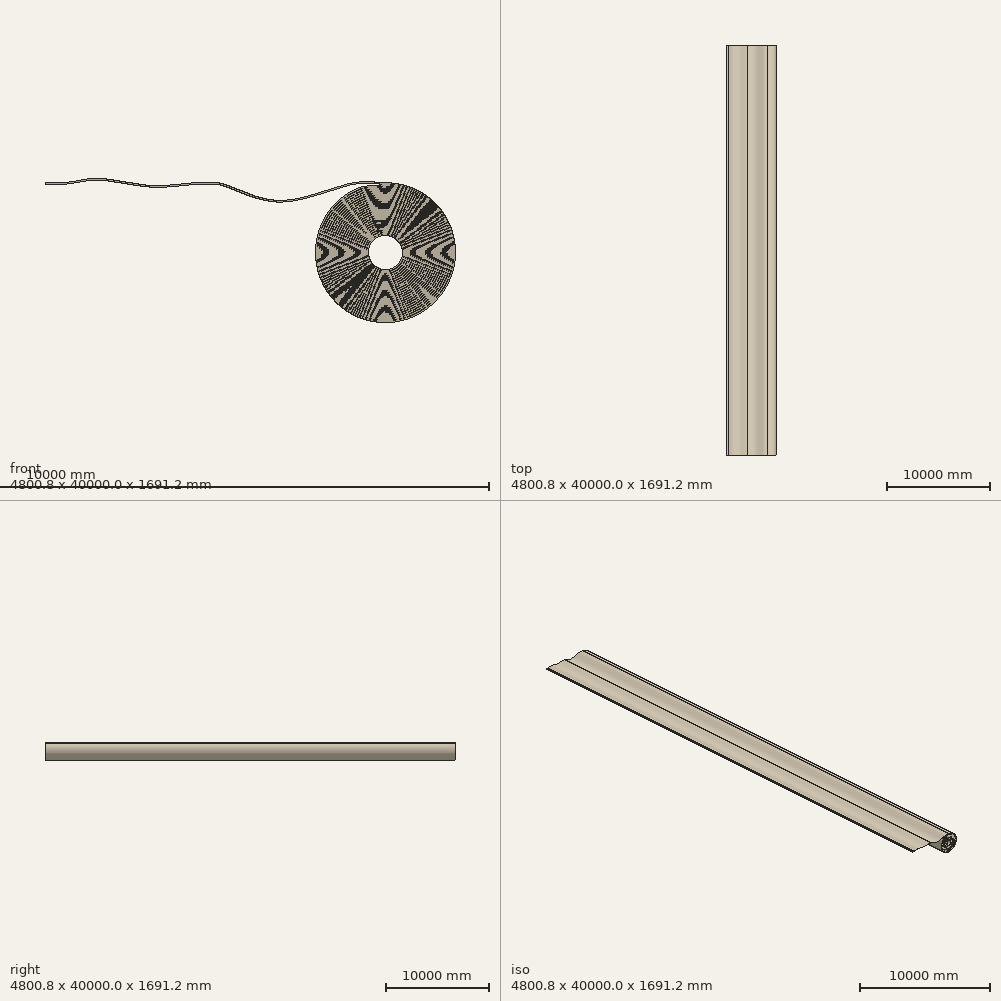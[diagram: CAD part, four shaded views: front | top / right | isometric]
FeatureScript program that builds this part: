
annotation { "Feature Type Name" : "Feature", "Feature Type Description" : "" }
export const myFeature = defineFeature(function(context is Context, id is Id, definition is map)
    precondition{}
    {
        {
            var Q0;
            Q0=qCreatedBy(makeId("Front.planeOp"),FACE);
            var sketch = newSketch(context, id + "F0", { "sketchPlane" : qUnion([Q0])});
            skLineSegment(sketch, "E0", {"start": v(-1454.5, 0) * mm, "end": v(-1283.8, 0) * mm});
            skFitSpline(sketch, "E1", {"points": [v(545.5, 0) * mm, v(1228.86, -205.21) * mm, v(2155.56, 0) * mm, v(2545.5, 0) * mm], "startDerivative": vector(1068.45, 0) * mm, "endDerivative": vector(1156.29, 20.17) * mm});
            skArc(sketch, "E2", {"start": v(2242.52, -51.78) * mm, "mid": v(2661.05, -1588.33) * mm, "end": v(2545.5, 0) * mm});
            skArc(sketch, "E3", {"start": v(2480.79, -605.01) * mm, "mid": v(2539.7, -999.32) * mm, "end": v(2545.3, -600.67) * mm});
            skArc(sketch, "E4", {"start": v(2252.73, -74.65) * mm, "mid": v(2716.15, -1551.15) * mm, "end": v(2422.52, -31.75) * mm});
            skArc(sketch, "E5", {"start": v(2265.35, -96.62) * mm, "mid": v(2704.7, -1528.24) * mm, "end": v(2432.73, -55.63) * mm});
            skArc(sketch, "E6", {"start": v(2296.13, -191.88) * mm, "mid": v(2671.8, -1433.27) * mm, "end": v(2468.1, -152.38) * mm});
            skArc(sketch, "E7", {"start": v(2311.7, -239.45) * mm, "mid": v(2656.21, -1385.53) * mm, "end": v(2483.8, -201.27) * mm});
            skArc(sketch, "E8", {"start": v(2330.08, -285.95) * mm, "mid": v(2638.4, -1338.22) * mm, "end": v(2501.1, -250.35) * mm});
            skArc(sketch, "E9", {"start": v(2270.13, -121.53) * mm, "mid": v(2696.14, -1504.6) * mm, "end": v(2445.35, -79.3) * mm});
            skArc(sketch, "E10", {"start": v(2278.47, -145.1) * mm, "mid": v(2689.56, -1480.46) * mm, "end": v(2450.13, -103.92) * mm});
            skArc(sketch, "E11", {"start": v(2288.1, -168.19) * mm, "mid": v(2680.58, -1456.9) * mm, "end": v(2458.47, -128.18) * mm});
            skArc(sketch, "E12", {"start": v(2303.8, -215.7) * mm, "mid": v(2663.97, -1409.41) * mm, "end": v(2476.13, -176.78) * mm});
            skArc(sketch, "E13", {"start": v(2321.1, -262.62) * mm, "mid": v(2647.56, -1361.83) * mm, "end": v(2491.7, -225.8) * mm});
            skArc(sketch, "E14", {"start": v(2334.03, -311.23) * mm, "mid": v(2632.06, -1314) * mm, "end": v(2510.08, -275.02) * mm});
            skArc(sketch, "E15", {"start": v(2348.93, -332.28) * mm, "mid": v(2622.45, -1290.43) * mm, "end": v(2514.03, -299.92) * mm});
            skArc(sketch, "E16", {"start": v(2357.64, -355.71) * mm, "mid": v(2610.7, -1267.2) * mm, "end": v(2528.93, -324.78) * mm});
            skArc(sketch, "E17", {"start": v(2366.27, -379.18) * mm, "mid": v(2602.03, -1243.35) * mm, "end": v(2537.64, -349.91) * mm});
            skArc(sketch, "E18", {"start": v(2368.44, -405.17) * mm, "mid": v(2596.8, -1218.88) * mm, "end": v(2546.27, -375.24) * mm});
            skArc(sketch, "E19", {"start": v(2375.13, -429.42) * mm, "mid": v(2592.39, -1194.27) * mm, "end": v(2548.44, -400.38) * mm});
            skArc(sketch, "E20", {"start": v(2380.2, -454.4) * mm, "mid": v(2586.6, -1169.89) * mm, "end": v(2555.13, -425.88) * mm});
            skArc(sketch, "E21", {"start": v(2394.28, -475.61) * mm, "mid": v(2576.79, -1146.1) * mm, "end": v(2560.2, -451.42) * mm});
            skArc(sketch, "E22", {"start": v(2398.74, -500.84) * mm, "mid": v(2577.57, -1120.7) * mm, "end": v(2554.28, -475.98) * mm});
            skArc(sketch, "E23", {"start": v(2403.66, -525.97) * mm, "mid": v(2572.98, -1096.11) * mm, "end": v(2558.74, -501.53) * mm});
            skArc(sketch, "E24", {"start": v(2417.42, -547.23) * mm, "mid": v(2563.37, -1072.26) * mm, "end": v(2563.66, -527.32) * mm});
            skArc(sketch, "E25", {"start": v(2431.23, -568.54) * mm, "mid": v(2559.32, -1047.58) * mm, "end": v(2557.42, -551.72) * mm});
            skArc(sketch, "E26", {"start": v(2445.3, -589.85) * mm, "mid": v(2555.12, -1022.91) * mm, "end": v(2551.23, -576.16) * mm});
            skFitSpline(sketch, "E27", {"points": [v(2242.52, -51.78) * mm, v(2422.52, -31.75) * mm], "startDerivative": vector(183.93, 61.4) * mm, "endDerivative": vector(153.02, 25.9) * mm});
            skFitSpline(sketch, "E28", {"points": [v(2252.73, -74.65) * mm, v(2432.73, -55.63) * mm], "startDerivative": vector(180.32, 59.73) * mm, "endDerivative": vector(156.49, 25.3) * mm});
            skFitSpline(sketch, "E29", {"points": [v(2265.35, -96.62) * mm, v(2445.35, -79.3) * mm], "startDerivative": vector(157.48, 51.92) * mm, "endDerivative": vector(138.8, 26.35) * mm});
            skFitSpline(sketch, "E30", {"points": [v(2270.13, -121.53) * mm, v(2450.13, -103.92) * mm], "startDerivative": vector(147.61, 49.78) * mm, "endDerivative": vector(149.7, 21.86) * mm});
            skFitSpline(sketch, "E31", {"points": [v(2278.47, -145.1) * mm, v(2458.47, -128.18) * mm], "startDerivative": vector(145.35, 49.03) * mm, "endDerivative": vector(142.65, 19.55) * mm});
            skFitSpline(sketch, "E32", {"points": [v(2288.1, -168.19) * mm, v(2468.1, -152.38) * mm], "startDerivative": vector(136.5, 46) * mm, "endDerivative": vector(134.79, 16.86) * mm});
            skFitSpline(sketch, "E33", {"points": [v(2296.13, -191.88) * mm, v(2476.13, -176.78) * mm], "startDerivative": vector(141.39, 47.43) * mm, "endDerivative": vector(141.01, 16.75) * mm});
            skFitSpline(sketch, "E34", {"points": [v(2303.8, -215.7) * mm, v(2483.8, -201.27) * mm], "startDerivative": vector(129, 43.84) * mm, "endDerivative": vector(124.28, 13.17) * mm});
            skFitSpline(sketch, "E35", {"points": [v(2311.7, -239.45) * mm, v(2491.7, -225.8) * mm], "startDerivative": vector(119.14, 40.9) * mm, "endDerivative": vector(114.47, 10.73) * mm});
            skFitSpline(sketch, "E36", {"points": [v(2321.1, -262.62) * mm, v(2501.1, -250.35) * mm], "startDerivative": vector(112.96, 38.72) * mm, "endDerivative": vector(112.88, 9.06) * mm});
            skFitSpline(sketch, "E37", {"points": [v(2330.08, -285.95) * mm, v(2510.08, -275.02) * mm], "startDerivative": vector(97.73, 33.85) * mm, "endDerivative": vector(114.93, 7.76) * mm});
            skFitSpline(sketch, "E38", {"points": [v(2334.03, -311.23) * mm, v(2514.03, -299.92) * mm], "startDerivative": vector(96.73, 34.47) * mm, "endDerivative": vector(104.3, 6.2) * mm});
            skFitSpline(sketch, "E39", {"points": [v(2348.93, -332.28) * mm, v(2528.93, -324.78) * mm], "startDerivative": vector(104.34, 35.26) * mm, "endDerivative": vector(98.4, 2.85) * mm});
            skFitSpline(sketch, "E40", {"points": [v(2357.64, -355.71) * mm, v(2537.64, -349.91) * mm], "startDerivative": vector(81.1, 28.03) * mm, "endDerivative": vector(89.55, 0.7) * mm});
            skFitSpline(sketch, "E41", {"points": [v(2366.27, -379.18) * mm, v(2546.27, -375.24) * mm], "startDerivative": vector(85.71, 29.35) * mm, "endDerivative": vector(93.78, -0.96) * mm});
            skFitSpline(sketch, "E42", {"points": [v(2368.44, -405.17) * mm, v(2548.44, -400.38) * mm], "startDerivative": vector(85.5, 30.71) * mm, "endDerivative": vector(80.17, -1.76) * mm});
            skFitSpline(sketch, "E43", {"points": [v(2375.13, -429.42) * mm, v(2555.13, -425.88) * mm], "startDerivative": vector(81.72, 29.94) * mm, "endDerivative": vector(84.05, -3.33) * mm});
            skFitSpline(sketch, "E44", {"points": [v(2380.2, -454.4) * mm, v(2560.2, -451.42) * mm], "startDerivative": vector(80.36, 30.43) * mm, "endDerivative": vector(77.15, -4.65) * mm});
            skFitSpline(sketch, "E45", {"points": [v(2394.28, -475.61) * mm, v(2554.28, -475.98) * mm], "startDerivative": vector(76.12, 27.62) * mm, "endDerivative": vector(69.22, -3.51) * mm});
            skFitSpline(sketch, "E46", {"points": [v(2398.74, -500.84) * mm, v(2558.74, -501.53) * mm], "startDerivative": vector(68.77, 26.32) * mm, "endDerivative": vector(77.85, -5.07) * mm});
            skFitSpline(sketch, "E47", {"points": [v(2403.66, -525.97) * mm, v(2563.66, -527.32) * mm], "startDerivative": vector(70.8, 28.17) * mm, "endDerivative": vector(68.79, -6.52) * mm});
            skFitSpline(sketch, "E48", {"points": [v(2417.42, -547.23) * mm, v(2557.42, -551.72) * mm], "startDerivative": vector(68.59, 26.01) * mm, "endDerivative": vector(69.01, -5.45) * mm});
            skFitSpline(sketch, "E49", {"points": [v(2431.23, -568.54) * mm, v(2551.23, -576.16) * mm], "startDerivative": vector(61.45, 22.18) * mm, "endDerivative": vector(64.9, -4.09) * mm});
            skFitSpline(sketch, "E50", {"points": [v(2445.3, -589.85) * mm, v(2545.3, -600.67) * mm], "startDerivative": vector(53.88, 18.22) * mm, "endDerivative": vector(56.63, -2.72) * mm});
            skFitSpline(sketch, "E51", {"points": [v(545.5, 0) * mm, v(290.37, 0) * mm, v(-223.77, -32.7) * mm, v(-866.4, 51.44) * mm, v(-1283.8, 0) * mm], "startDerivative": vector(-2021.3, 0) * mm, "endDerivative": vector(-2066.32, 0) * mm});
            skSolve(sketch);
        }
        {
            var Q0;
            Q0=sQuery(id+"F0.wireOp",VERTEX,"E0.start");
            var Q1;
            Q1=qCreatedBy(makeId("Right.planeOp"),FACE);
            cPlane(context, id + "F1", {"entities" : qUnion([Q0, Q1]), "cplaneType" : CPlaneType.PLANE_POINT, "offset" : 25 * mm, "width" : 150 * mm, "height" : 150 * mm});
        }
        {
            var Q0;
            Q0=qCreatedBy(id+"F1.planeOp",FACE);
            var sketch = newSketch(context, id + "F2", { "sketchPlane" : qUnion([Q0])});
            skLineSegment(sketch, "E52.bottom", {"start": v(0, 0) * mm, "end": v(40000, 0) * mm});
            skLineSegment(sketch, "E52.top", {"start": v(0, 20) * mm, "end": v(40000, 20) * mm});
            skLineSegment(sketch, "E52.left", {"start": v(0, 0) * mm, "end": v(0, 20) * mm});
            skLineSegment(sketch, "E52.right", {"start": v(40000, 0) * mm, "end": v(40000, 20) * mm});
            skSolve(sketch);
        }
        {
            var Q0;
            Q0=makeQuery(id+"F2.imprint","IMPRINT",FACE,{"disambiguationData":[TD([[makeQuery(id+"F2.imprint","IMPRINT",EDGE,{"derivedFrom":sQuery(id+"F2.wireOp",EDGE,"E52.bottom")}),1.0]])]});
            var Q1;
            Q1=sQuery(id+"F0.wireOp",EDGE,"E0");
            var Q2;
            Q2=sQuery(id+"F0.wireOp",EDGE,"E1");
            var Q3;
            Q3=sQuery(id+"F0.wireOp",EDGE,"E2");
            var Q4;
            Q4=sQuery(id+"F0.wireOp",EDGE,"E27");
            var Q5;
            Q5=sQuery(id+"F0.wireOp",EDGE,"E4");
            var Q6;
            Q6=sQuery(id+"F0.wireOp",EDGE,"E28");
            var Q7;
            Q7=sQuery(id+"F0.wireOp",EDGE,"E5");
            var Q8;
            Q8=sQuery(id+"F0.wireOp",EDGE,"E29");
            var Q9;
            Q9=sQuery(id+"F0.wireOp",EDGE,"E9");
            var Q10;
            Q10=sQuery(id+"F0.wireOp",EDGE,"E30");
            var Q11;
            Q11=sQuery(id+"F0.wireOp",EDGE,"E10");
            var Q12;
            Q12=sQuery(id+"F0.wireOp",EDGE,"E31");
            var Q13;
            Q13=sQuery(id+"F0.wireOp",EDGE,"E11");
            var Q14;
            Q14=sQuery(id+"F0.wireOp",EDGE,"E32");
            var Q15;
            Q15=sQuery(id+"F0.wireOp",EDGE,"E6");
            var Q16;
            Q16=sQuery(id+"F0.wireOp",EDGE,"E33");
            var Q17;
            Q17=sQuery(id+"F0.wireOp",EDGE,"E12");
            var Q18;
            Q18=sQuery(id+"F0.wireOp",EDGE,"E34");
            var Q19;
            Q19=sQuery(id+"F0.wireOp",EDGE,"E7");
            var Q20;
            Q20=sQuery(id+"F0.wireOp",EDGE,"E35");
            var Q21;
            Q21=sQuery(id+"F0.wireOp",EDGE,"E13");
            var Q22;
            Q22=sQuery(id+"F0.wireOp",EDGE,"E36");
            var Q23;
            Q23=sQuery(id+"F0.wireOp",EDGE,"E8");
            var Q24;
            Q24=sQuery(id+"F0.wireOp",EDGE,"E37");
            var Q25;
            Q25=sQuery(id+"F0.wireOp",EDGE,"E14");
            var Q26;
            Q26=sQuery(id+"F0.wireOp",EDGE,"E38");
            var Q27;
            Q27=sQuery(id+"F0.wireOp",EDGE,"E36");
            var Q28;
            Q28=sQuery(id+"F0.wireOp",EDGE,"E15");
            var Q29;
            Q29=sQuery(id+"F0.wireOp",EDGE,"E39");
            var Q30;
            Q30=sQuery(id+"F0.wireOp",EDGE,"E16");
            var Q31;
            Q31=sQuery(id+"F0.wireOp",EDGE,"E40");
            var Q32;
            Q32=sQuery(id+"F0.wireOp",EDGE,"E17");
            var Q33;
            Q33=sQuery(id+"F0.wireOp",EDGE,"E41");
            var Q34;
            Q34=sQuery(id+"F0.wireOp",EDGE,"E18");
            var Q35;
            Q35=sQuery(id+"F0.wireOp",EDGE,"E42");
            var Q36;
            Q36=sQuery(id+"F0.wireOp",EDGE,"E19");
            var Q37;
            Q37=sQuery(id+"F0.wireOp",EDGE,"E43");
            var Q38;
            Q38=sQuery(id+"F0.wireOp",EDGE,"E20");
            var Q39;
            Q39=sQuery(id+"F0.wireOp",EDGE,"E44");
            var Q40;
            Q40=sQuery(id+"F0.wireOp",EDGE,"E21");
            var Q41;
            Q41=sQuery(id+"F0.wireOp",EDGE,"E45");
            var Q42;
            Q42=sQuery(id+"F0.wireOp",EDGE,"E22");
            var Q43;
            Q43=sQuery(id+"F0.wireOp",EDGE,"E46");
            var Q44;
            Q44=sQuery(id+"F0.wireOp",EDGE,"E23");
            var Q45;
            Q45=sQuery(id+"F0.wireOp",EDGE,"E47");
            var Q46;
            Q46=sQuery(id+"F0.wireOp",EDGE,"E24");
            var Q47;
            Q47=sQuery(id+"F0.wireOp",EDGE,"E48");
            var Q48;
            Q48=sQuery(id+"F0.wireOp",EDGE,"E25");
            var Q49;
            Q49=sQuery(id+"F0.wireOp",EDGE,"E49");
            var Q50;
            Q50=sQuery(id+"F0.wireOp",EDGE,"E26");
            var Q51;
            Q51=sQuery(id+"F0.wireOp",EDGE,"E50");
            var Q52;
            Q52=sQuery(id+"F0.wireOp",EDGE,"E3");
            var Q53;
            Q53=sQuery(id+"F0.wireOp",EDGE,"E51");
            sweep(context, id + "F3", {"profiles" : qUnion([Q0]), "path" : qUnion([Q1, Q2, Q3, Q4, Q5, Q6, Q7, Q8, Q9, Q10, Q11, Q12, Q13, Q14, Q15, Q16, Q17, Q18, Q19, Q20, Q21, Q22, Q23, Q24, Q25, Q26, Q27, Q28, Q29, Q30, Q31, Q32, Q33, Q34, Q35, Q36, Q37, Q38, Q39, Q40, Q41, Q42, Q43, Q44, Q45, Q46, Q47, Q48, Q49, Q50, Q51, Q52, Q53])});
        }
        {
            var Q0;
            Q0=makeQuery(id+"F3.opSweep","SWEPT_FACE",FACE,{"disambiguationData":[OSD([sQuery(id+"F0.wireOp",EDGE,"E0"),sQuery(id+"F2.wireOp",EDGE,"E52.bottom")])]});
            var sketch = newSketch(context, id + "F4", { "sketchPlane" : qUnion([Q0])});
            skCircle(sketch, "E53", {"center": v(-1369.14, -39900) * mm, "radius": 17.5 * mm});
            skPoint(sketch, "E53.centerSnap0", {"position": v(-1369.14, -40000) * mm});
            skCircle(sketch, "E54.0.1.0", {"center": v(-1369.14, -34250) * mm, "radius": 17.5 * mm});
            skCircle(sketch, "E54.0.2.0", {"center": v(-1369.14, -28600) * mm, "radius": 17.5 * mm});
            skCircle(sketch, "E54.0.3.0", {"center": v(-1369.14, -22950) * mm, "radius": 17.5 * mm});
            skCircle(sketch, "E54.0.4.0", {"center": v(-1369.14, -17300) * mm, "radius": 17.5 * mm});
            skCircle(sketch, "E54.0.5.0", {"center": v(-1369.14, -11650) * mm, "radius": 17.5 * mm});
            skCircle(sketch, "E54.0.6.0", {"center": v(-1369.14, -6000) * mm, "radius": 17.5 * mm});
            skCircle(sketch, "E54.0.7.0", {"center": v(-1369.14, -350) * mm, "radius": 17.5 * mm});
            skLineSegment(sketch, "E54.direction1", {"start": v(-1369.14, -39900) * mm, "end": v(-1039.14, -39900) * mm, "construction": true});
            skLineSegment(sketch, "E54.direction2", {"start": v(-1369.14, -39900) * mm, "end": v(-1369.14, -34250) * mm, "construction": true});
            skSolve(sketch);
        }
        {
            var Q0;
            Q0 = qSketchRegion(id + "F4", true);
            extrude(context, id + "F5", {"entities" : qUnion([Q0]), "operationType" : NewBodyOperationType.REMOVE, "oppositeDirection" : true, "depth" : 25 * mm, "offsetDistance" : 25 * mm});
        }
    });
